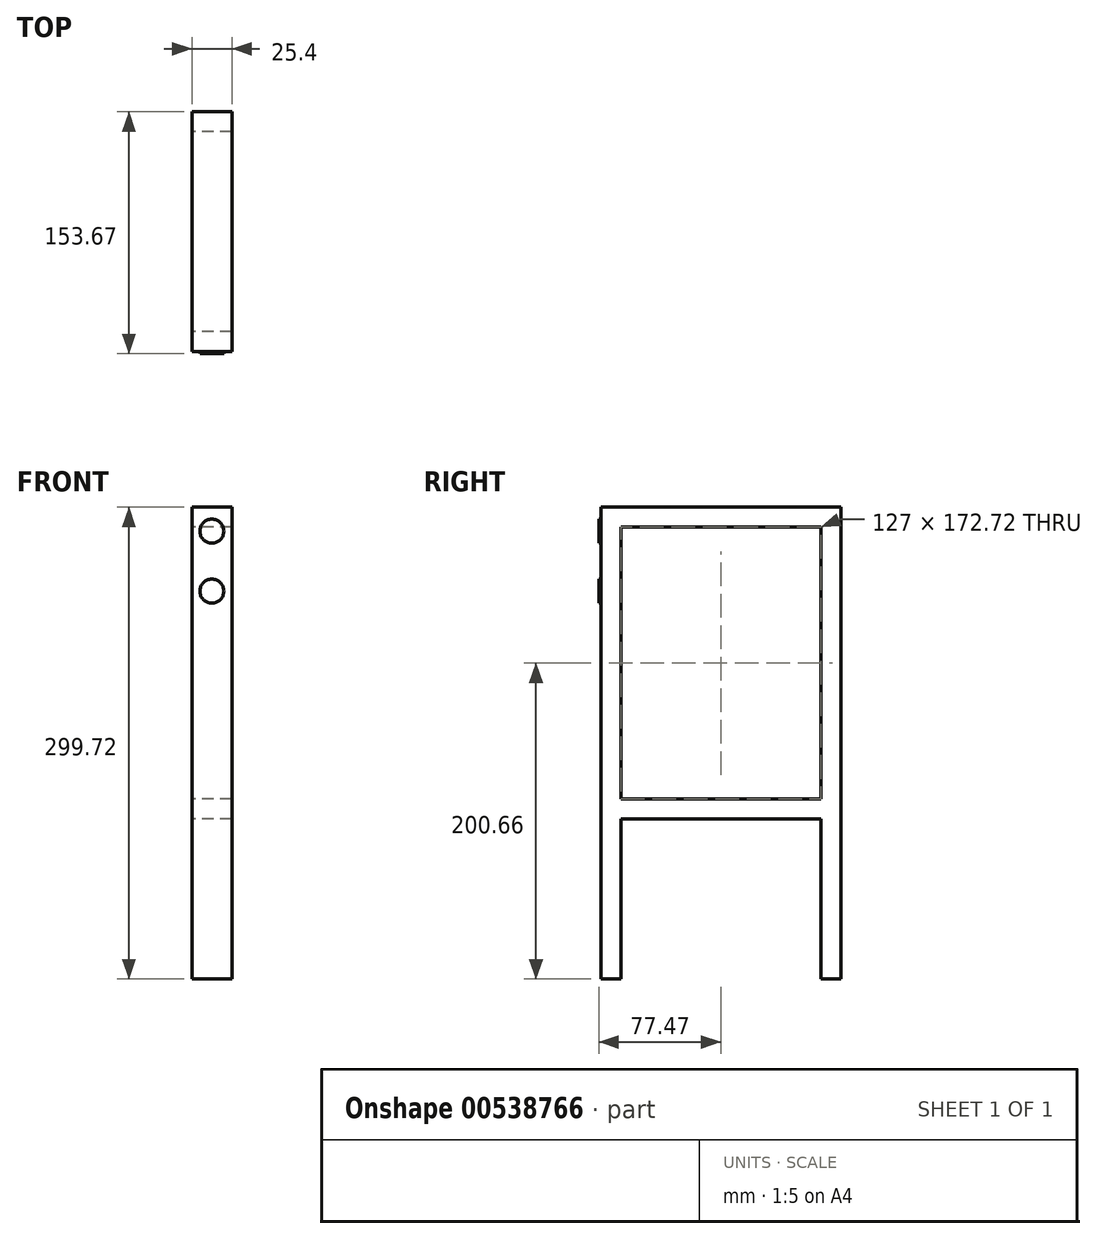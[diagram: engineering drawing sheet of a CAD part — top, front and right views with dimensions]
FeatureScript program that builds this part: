
annotation { "Feature Type Name" : "Feature", "Feature Type Description" : "" }
export const myFeature = defineFeature(function(context is Context, id is Id, definition is map)
    precondition{}
    {
        {
            var Q0;
            Q0=qCreatedBy(makeId("Right.planeOp"),FACE);
            var sketch = newSketch(context, id + "F0", { "sketchPlane" : qUnion([Q0])});
            skLineSegment(sketch, "E0.bottom", {"start": v(76.2, 149.86) * mm, "end": v(-76.2, 149.86) * mm});
            skLineSegment(sketch, "E0.top", {"start": v(76.2, -149.86) * mm, "end": v(-76.2, -149.86) * mm});
            skLineSegment(sketch, "E0.left", {"start": v(76.2, 149.86) * mm, "end": v(76.2, -149.86) * mm});
            skLineSegment(sketch, "E0.right", {"start": v(-76.2, 149.86) * mm, "end": v(-76.2, -149.86) * mm});
            skPoint(sketch, "E0.middle", {"position": v(0, 0) * mm});
            skLineSegment(sketch, "E1", {"start": v(-63.5, -149.86) * mm, "end": v(63.5, -149.86) * mm});
            skPoint(sketch, "E2", {"position": v(0, -149.86) * mm});
            skLineSegment(sketch, "E3", {"start": v(-63.5, -149.86) * mm, "end": v(-63.5, -48.26) * mm});
            skLineSegment(sketch, "E4", {"start": v(-63.5, -48.26) * mm, "end": v(63.5, -48.26) * mm});
            skLineSegment(sketch, "E5", {"start": v(63.5, -48.26) * mm, "end": v(63.5, -149.86) * mm});
            skLineSegment(sketch, "E6", {"start": v(0, 149.86) * mm, "end": v(0, 137.16) * mm, "construction": true});
            skPoint(sketch, "E6.endSnap0", {"position": v(0, 149.86) * mm});
            skLineSegment(sketch, "E7", {"start": v(0, 137.16) * mm, "end": v(63.5, 137.16) * mm});
            skLineSegment(sketch, "E8", {"start": v(63.5, 137.16) * mm, "end": v(63.5, -35.56) * mm});
            skLineSegment(sketch, "E9", {"start": v(63.5, -35.56) * mm, "end": v(-63.5, -35.56) * mm});
            skLineSegment(sketch, "E10", {"start": v(-63.5, -35.56) * mm, "end": v(-63.5, 137.16) * mm});
            skLineSegment(sketch, "E11", {"start": v(-63.5, 137.16) * mm, "end": v(0, 137.16) * mm});
            skSolve(sketch);
        }
        {
            var Q0;
            Q0=makeQuery(id+"F0.imprint","IMPRINT",FACE,{"disambiguationData":[TD([[makeQuery(id+"F0.imprint","IMPRINT",EDGE,{"derivedFrom":sQuery(id+"F0.wireOp",EDGE,"E0.bottom")}),1.0]])]});
            extrude(context, id + "F1", {"entities" : qUnion([Q0]), "endBound" : BoundingType.SYMMETRIC, "depth" : 25.4 * mm, "offsetDistance" : 25.4 * mm});
        }
        {
            var Q0;
            Q0=makeQuery(id+"F1.opExtrude","SWEPT_FACE",FACE,{"disambiguationData":[OSD([sQuery(id+"F0.wireOp",EDGE,"E0.right")])]});
            var sketch = newSketch(context, id + "F2", { "sketchPlane" : qUnion([Q0])});
            skPoint(sketch, "E12.endSnap0", {"position": v(0, -149.86) * mm});
            skLineSegment(sketch, "E13", {"start": v(0, 149.86) * mm, "end": v(0, 134.62) * mm, "construction": true});
            skPoint(sketch, "E13.endSnap0", {"position": v(0, 149.86) * mm});
            skLineSegment(sketch, "E14", {"start": v(0, -149.86) * mm, "end": v(0, 96.52) * mm, "construction": true});
            skCircle(sketch, "E15", {"center": v(0, 96.52) * mm, "radius": 7.62 * mm});
            skCircle(sketch, "E16", {"center": v(0, 134.62) * mm, "radius": 7.62 * mm});
            skSolve(sketch);
        }
        {
            var Q0;
            Q0 = qSketchRegion(id + "F2", true);
            extrude(context, id + "F3", {"entities" : qUnion([Q0]), "operationType" : NewBodyOperationType.ADD, "depth" : 1.27 * mm, "offsetDistance" : 25.4 * mm});
        }
    });
